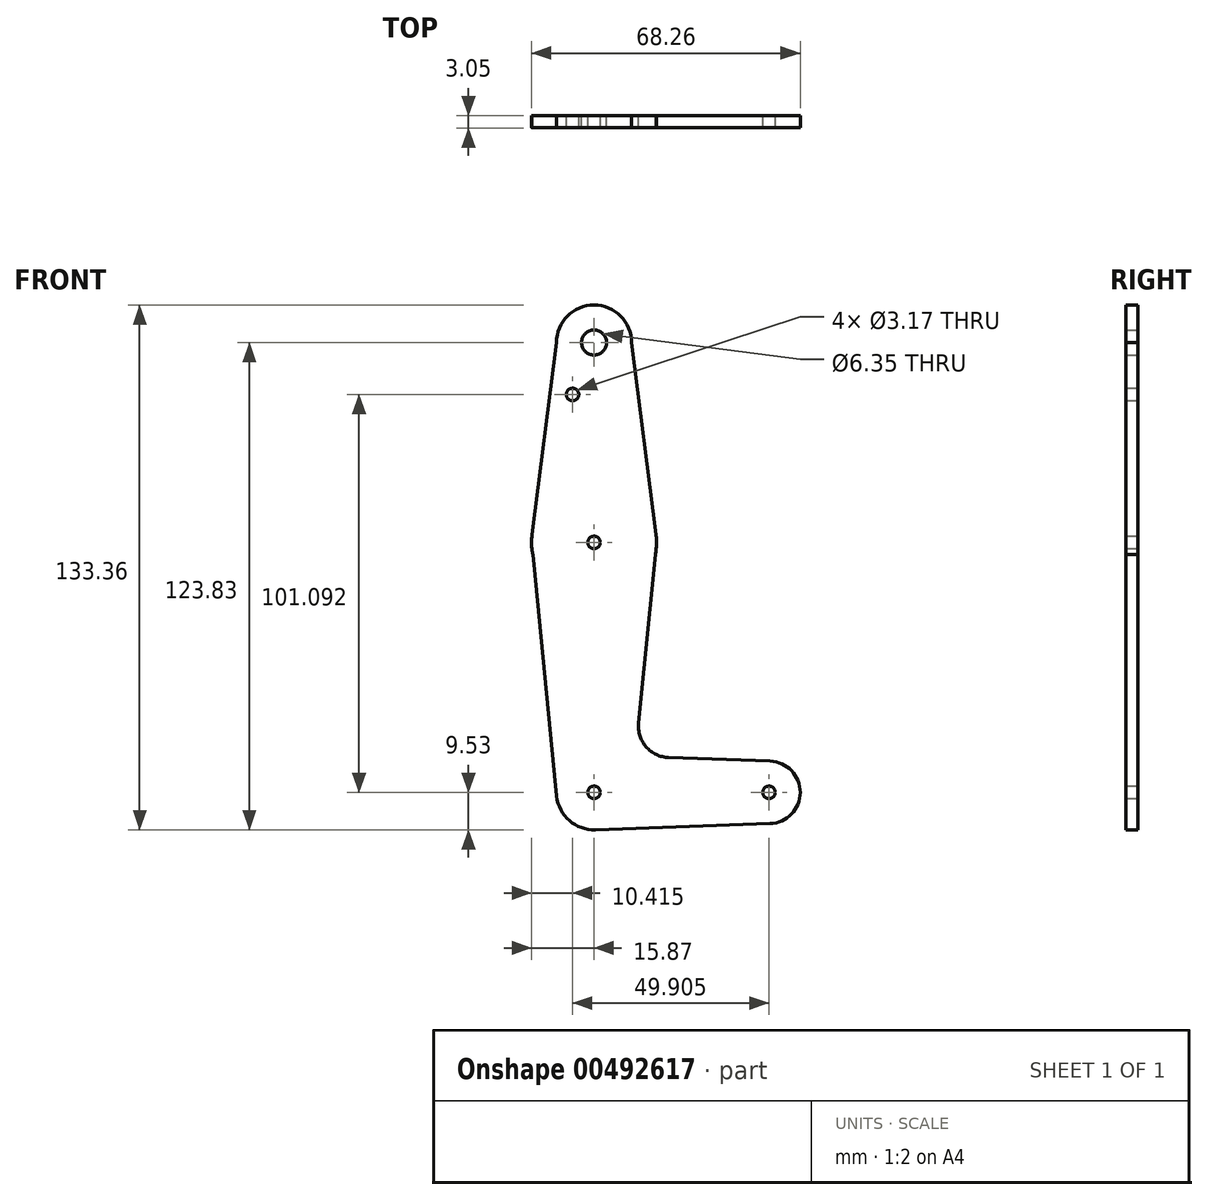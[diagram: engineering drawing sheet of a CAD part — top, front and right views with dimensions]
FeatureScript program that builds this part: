
annotation { "Feature Type Name" : "Feature", "Feature Type Description" : "" }
export const myFeature = defineFeature(function(context is Context, id is Id, definition is map)
    precondition{}
    {
        {
            var Q0;
            Q0=qCreatedBy(makeId("Front.planeOp"),FACE);
            var sketch = newSketch(context, id + "F0", { "sketchPlane" : qUnion([Q0])});
            skCircle(sketch, "E0", {"center": v(0, 114.3) * mm, "radius": 9.53 * mm});
            skCircle(sketch, "E1", {"center": v(0, 0) * mm, "radius": 9.53 * mm});
            skLineSegment(sketch, "E2", {"start": v(0, 114.3) * mm, "end": v(0, 0) * mm, "construction": true});
            skLineSegment(sketch, "E3", {"start": v(0, 0) * mm, "end": v(44.45, 0) * mm, "construction": true});
            skCircle(sketch, "E4", {"center": v(44.45, 0) * mm, "radius": 7.94 * mm});
            skLineSegment(sketch, "E5", {"start": v(18.94, 8.85) * mm, "end": v(44.73, 7.93) * mm});
            skLineSegment(sketch, "E6", {"start": v(44.73, -7.93) * mm, "end": v(0.34, -9.52) * mm});
            skCircle(sketch, "E7", {"center": v(0, 63.5) * mm, "radius": 15.88 * mm});
            skLineSegment(sketch, "E8", {"start": v(15.88, 63.5) * mm, "end": v(11.32, 17.58) * mm});
            skLineSegment(sketch, "E9", {"start": v(-15.87, 63.5) * mm, "end": v(-9.48, -0.94) * mm});
            skLineSegment(sketch, "E10", {"start": v(-9.53, 114.3) * mm, "end": v(-15.75, 65.5) * mm});
            skLineSegment(sketch, "E11", {"start": v(9.52, 114.3) * mm, "end": v(15.75, 65.5) * mm});
            skCircle(sketch, "E12", {"center": v(0, 63.5) * mm, "radius": 1.59 * mm});
            skCircle(sketch, "E13", {"center": v(0, 0) * mm, "radius": 1.59 * mm});
            skCircle(sketch, "E14", {"center": v(44.45, 0) * mm, "radius": 1.59 * mm});
            skCircle(sketch, "E15", {"center": v(-5.45, 101.1) * mm, "radius": 1.59 * mm});
            skArc(sketch, "E16.filletArc", {"start": v(11.32, 17.58) * mm, "mid": v(13.24, 11.57) * mm, "end": v(18.94, 8.85) * mm});
            skCircle(sketch, "E17", {"center": v(0, 114.3) * mm, "radius": 3.18 * mm});
            skSolve(sketch);
        }
        {
            var Q0;
            Q0 = qSketchRegion(id + "F0", true);
            extrude(context, id + "F1", {"entities" : qUnion([Q0]), "depth" : 3.05 * mm});
        }
    });
